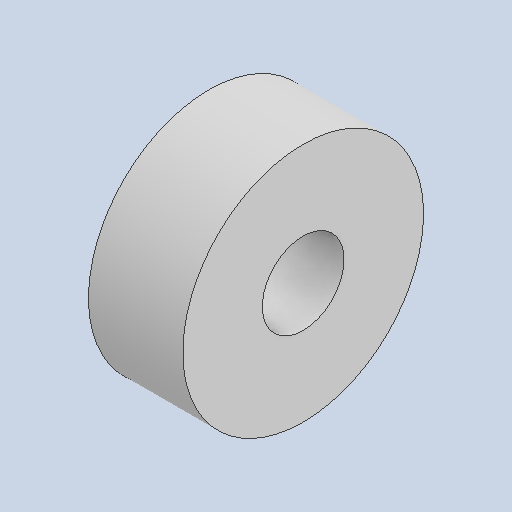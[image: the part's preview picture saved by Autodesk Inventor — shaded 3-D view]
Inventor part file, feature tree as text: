
AUTODESK INVENTOR PART (.ipt)
format: ipt  version: 2023 (Build 270158000, 158)  size: 92,672 bytes
history: native  units: in
note: dims shown in document units (in); Inventor stores cm internally (conversion verified against a paired STEP export)
features: other x3, sketch x1
ambient origin geometry x8: Origin, YZ Plane, XZ Plane, XY Plane, X Axis, Y Axis, Z Axis, Center Point
bodies: Solid1 (feature_tree)
feature tree (4):
  other  "vexbearing.ipt"
  other  "Solid1::vexbearing.ipt"
  other  "TaggingFeature1"
  sketch  "Sketch1"  dims[d0=0.3937in]
